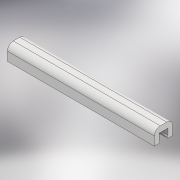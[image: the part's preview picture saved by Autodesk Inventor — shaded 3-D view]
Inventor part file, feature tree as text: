
AUTODESK INVENTOR PART (.ipt)
format: ipt  version: 2018.2 (Build 222227000, 227)  size: 126,976 bytes
history: native  units: mm
features: extrude x1, fillet x1, sketch x1
ambient origin geometry x8: Origin, YZ Plane, XZ Plane, XY Plane, X Axis, Y Axis, Z Axis, Center Point
bodies: Solid1 (feature_tree)
feature tree (3):
  extrude  "Extrusion1"  Depth=2.0mm
  fillet  "Fillet1"  Radius=1.6mm
  sketch  "Sketch1"  dims[d0=3.0mm d1=2.0mm d2=1.6mm d3=1.6mm d4=0.3mm d5=3.0mm d6=2.0mm d7=50.0mm d8=0.0mm d9=2.0mm]
